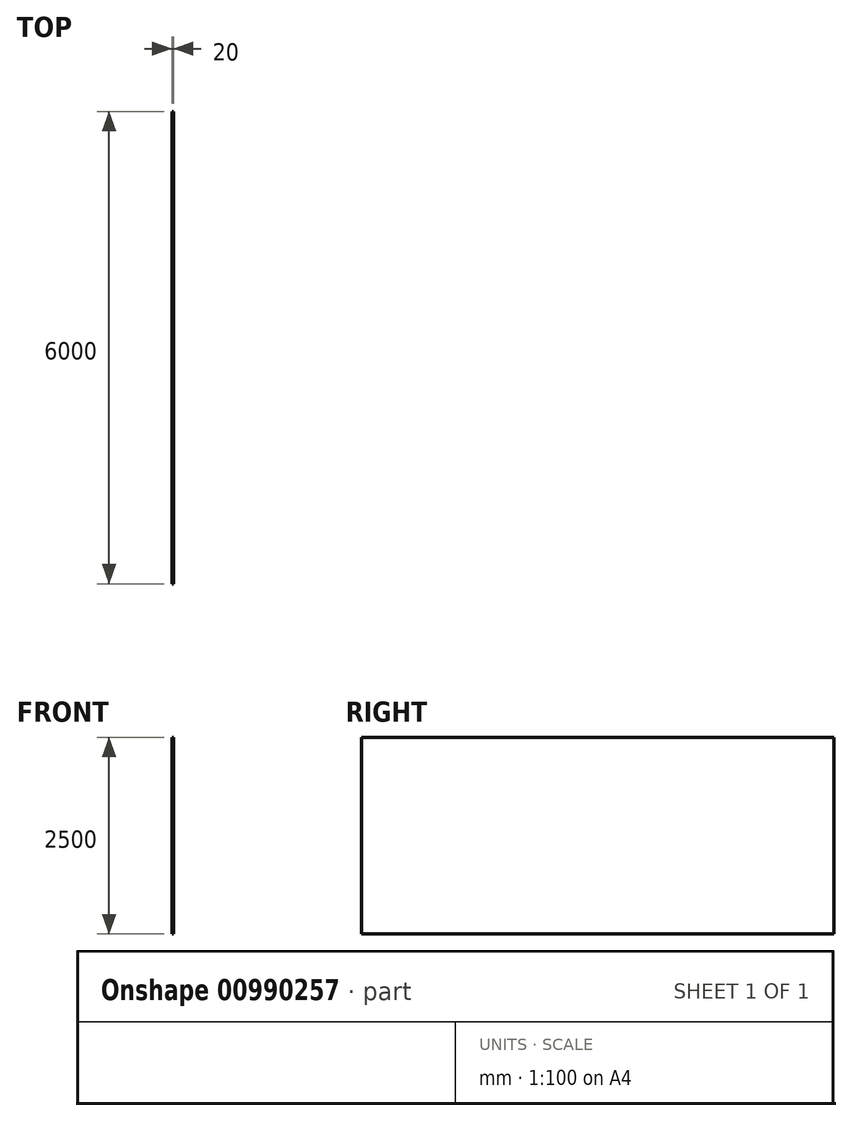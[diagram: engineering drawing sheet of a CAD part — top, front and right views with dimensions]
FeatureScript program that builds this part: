
annotation { "Feature Type Name" : "Feature", "Feature Type Description" : "" }
export const myFeature = defineFeature(function(context is Context, id is Id, definition is map)
    precondition{}
    {
        {
            var Q0;
            Q0=qCreatedBy(makeId("Right.planeOp"),FACE);
            var sketch = newSketch(context, id + "F0", { "sketchPlane" : qUnion([Q0])});
            skLineSegment(sketch, "E0.bottom", {"start": v(3543.6, 1247.75) * mm, "end": v(-2456.4, 1247.75) * mm});
            skLineSegment(sketch, "E0.top", {"start": v(3543.6, -1252.25) * mm, "end": v(-2456.4, -1252.25) * mm});
            skLineSegment(sketch, "E0.left", {"start": v(3543.6, 1247.75) * mm, "end": v(3543.6, -1252.25) * mm});
            skLineSegment(sketch, "E0.right", {"start": v(-2456.4, 1247.75) * mm, "end": v(-2456.4, -1252.25) * mm});
            skSolve(sketch);
        }
        {
            var Q0;
            Q0=makeQuery(id+"F0.imprint","IMPRINT",FACE,{"disambiguationData":[TD([[makeQuery(id+"F0.imprint","IMPRINT",EDGE,{"derivedFrom":sQuery(id+"F0.wireOp",EDGE,"E0.bottom")}),1.0]])]});
            extrude(context, id + "F1", {"entities" : qUnion([Q0]), "depth" : 20 * mm, "offsetDistance" : 25 * mm});
        }
    });
